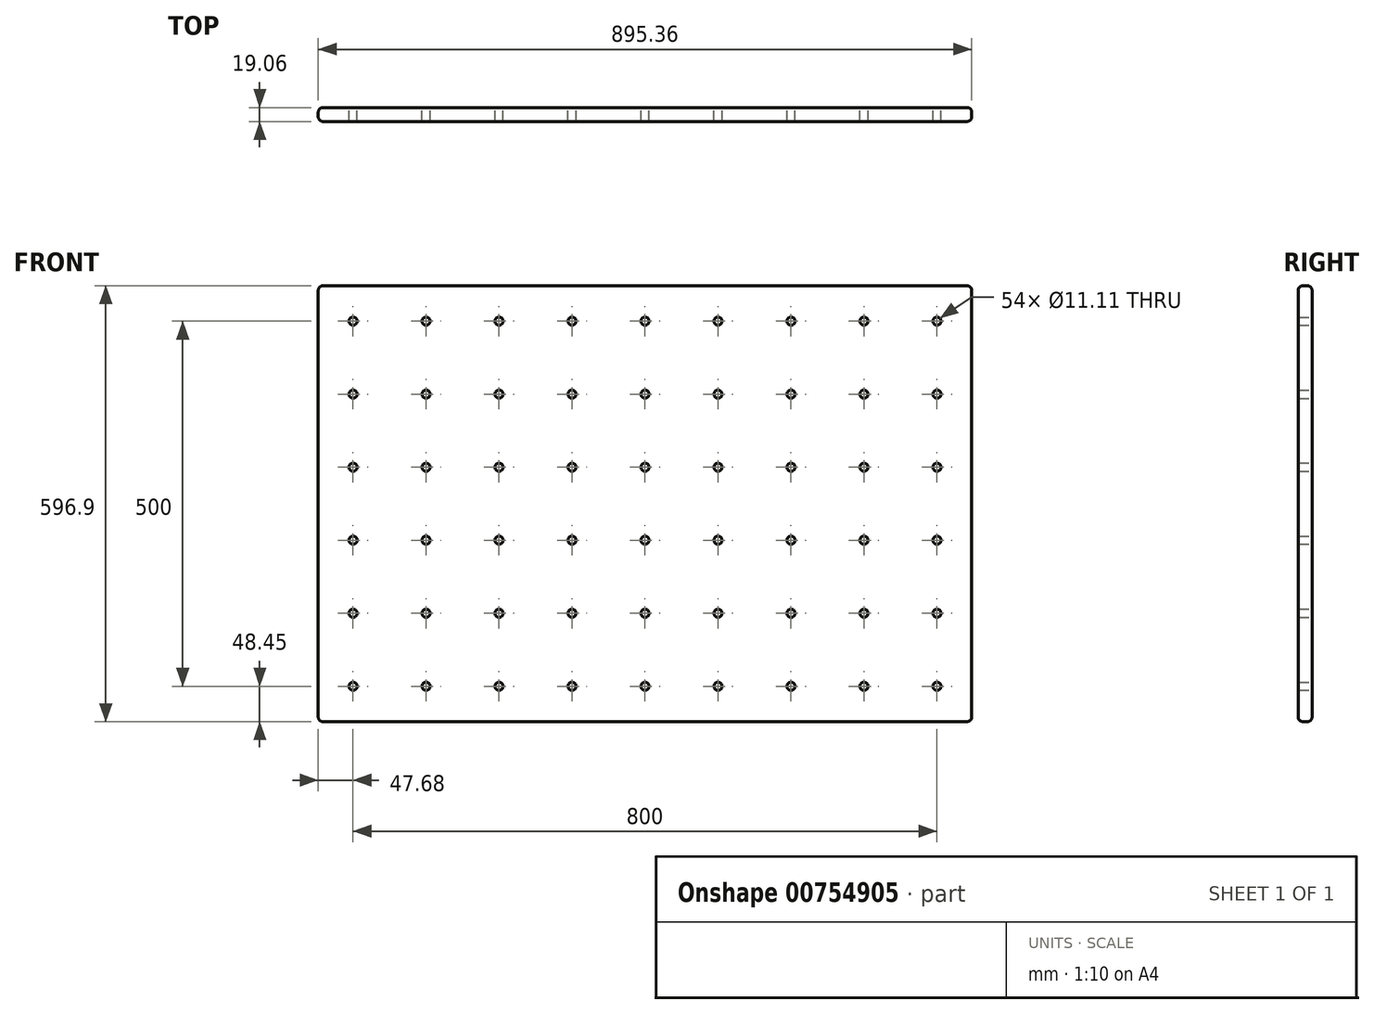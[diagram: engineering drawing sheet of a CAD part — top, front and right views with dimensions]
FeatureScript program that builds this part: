
annotation { "Feature Type Name" : "Feature", "Feature Type Description" : "" }
export const myFeature = defineFeature(function(context is Context, id is Id, definition is map)
    precondition{}
    {
        {
            var Q0;
            Q0=qCreatedBy(makeId("Front.planeOp"),FACE);
            var sketch = newSketch(context, id + "F0", { "sketchPlane" : qUnion([Q0])});
            skLineSegment(sketch, "E0.bottom", {"start": v(-447.68, 298.45) * mm, "end": v(447.68, 298.45) * mm});
            skLineSegment(sketch, "E0.top", {"start": v(-447.68, -298.45) * mm, "end": v(447.67, -298.45) * mm});
            skLineSegment(sketch, "E0.left", {"start": v(-447.68, 298.45) * mm, "end": v(-447.68, -298.45) * mm});
            skLineSegment(sketch, "E0.right", {"start": v(447.68, 298.45) * mm, "end": v(447.67, -298.45) * mm});
            skCircle(sketch, "E1", {"center": v(400, -250) * mm, "radius": 5.56 * mm});
            skCircle(sketch, "E2.0.1.0", {"center": v(400, -150) * mm, "radius": 5.56 * mm});
            skCircle(sketch, "E2.0.2.0", {"center": v(400, -50) * mm, "radius": 5.56 * mm});
            skCircle(sketch, "E2.0.3.0", {"center": v(400, 50) * mm, "radius": 5.56 * mm});
            skCircle(sketch, "E2.0.4.0", {"center": v(400, 150) * mm, "radius": 5.56 * mm});
            skCircle(sketch, "E2.0.5.0", {"center": v(400, 250) * mm, "radius": 5.56 * mm});
            skCircle(sketch, "E2.1.0.0", {"center": v(300, -250) * mm, "radius": 5.56 * mm});
            skCircle(sketch, "E2.1.1.0", {"center": v(300, -150) * mm, "radius": 5.56 * mm});
            skCircle(sketch, "E2.1.2.0", {"center": v(300, -50) * mm, "radius": 5.56 * mm});
            skCircle(sketch, "E2.1.3.0", {"center": v(300, 50) * mm, "radius": 5.56 * mm});
            skCircle(sketch, "E2.1.4.0", {"center": v(300, 150) * mm, "radius": 5.56 * mm});
            skCircle(sketch, "E2.1.5.0", {"center": v(300, 250) * mm, "radius": 5.56 * mm});
            skCircle(sketch, "E2.2.0.0", {"center": v(200, -250) * mm, "radius": 5.56 * mm});
            skCircle(sketch, "E2.2.1.0", {"center": v(200, -150) * mm, "radius": 5.56 * mm});
            skCircle(sketch, "E2.2.2.0", {"center": v(200, -50) * mm, "radius": 5.56 * mm});
            skCircle(sketch, "E2.2.3.0", {"center": v(200, 50) * mm, "radius": 5.56 * mm});
            skCircle(sketch, "E2.2.4.0", {"center": v(200, 150) * mm, "radius": 5.56 * mm});
            skCircle(sketch, "E2.2.5.0", {"center": v(200, 250) * mm, "radius": 5.56 * mm});
            skCircle(sketch, "E2.3.0.0", {"center": v(100, -250) * mm, "radius": 5.56 * mm});
            skCircle(sketch, "E2.3.1.0", {"center": v(100, -150) * mm, "radius": 5.56 * mm});
            skCircle(sketch, "E2.3.2.0", {"center": v(100, -50) * mm, "radius": 5.56 * mm});
            skCircle(sketch, "E2.3.3.0", {"center": v(100, 50) * mm, "radius": 5.56 * mm});
            skCircle(sketch, "E2.3.4.0", {"center": v(100, 150) * mm, "radius": 5.56 * mm});
            skCircle(sketch, "E2.3.5.0", {"center": v(100, 250) * mm, "radius": 5.56 * mm});
            skCircle(sketch, "E2.4.0.0", {"center": v(0, -250) * mm, "radius": 5.56 * mm});
            skCircle(sketch, "E2.4.1.0", {"center": v(0, -150) * mm, "radius": 5.56 * mm});
            skCircle(sketch, "E2.4.2.0", {"center": v(0, -50) * mm, "radius": 5.56 * mm});
            skCircle(sketch, "E2.4.3.0", {"center": v(0, 50) * mm, "radius": 5.56 * mm});
            skCircle(sketch, "E2.4.4.0", {"center": v(0, 150) * mm, "radius": 5.56 * mm});
            skCircle(sketch, "E2.4.5.0", {"center": v(0, 250) * mm, "radius": 5.56 * mm});
            skCircle(sketch, "E2.5.0.0", {"center": v(-100, -250) * mm, "radius": 5.56 * mm});
            skCircle(sketch, "E2.5.1.0", {"center": v(-100, -150) * mm, "radius": 5.56 * mm});
            skCircle(sketch, "E2.5.2.0", {"center": v(-100, -50) * mm, "radius": 5.56 * mm});
            skCircle(sketch, "E2.5.3.0", {"center": v(-100, 50) * mm, "radius": 5.56 * mm});
            skCircle(sketch, "E2.5.4.0", {"center": v(-100, 150) * mm, "radius": 5.56 * mm});
            skCircle(sketch, "E2.5.5.0", {"center": v(-100, 250) * mm, "radius": 5.56 * mm});
            skCircle(sketch, "E2.6.0.0", {"center": v(-200, -250) * mm, "radius": 5.56 * mm});
            skCircle(sketch, "E2.6.1.0", {"center": v(-200, -150) * mm, "radius": 5.56 * mm});
            skCircle(sketch, "E2.6.2.0", {"center": v(-200, -50) * mm, "radius": 5.56 * mm});
            skCircle(sketch, "E2.6.3.0", {"center": v(-200, 50) * mm, "radius": 5.56 * mm});
            skCircle(sketch, "E2.6.4.0", {"center": v(-200, 150) * mm, "radius": 5.56 * mm});
            skCircle(sketch, "E2.6.5.0", {"center": v(-200, 250) * mm, "radius": 5.56 * mm});
            skCircle(sketch, "E2.7.0.0", {"center": v(-300, -250) * mm, "radius": 5.56 * mm});
            skCircle(sketch, "E2.7.1.0", {"center": v(-300, -150) * mm, "radius": 5.56 * mm});
            skCircle(sketch, "E2.7.2.0", {"center": v(-300, -50) * mm, "radius": 5.56 * mm});
            skCircle(sketch, "E2.7.3.0", {"center": v(-300, 50) * mm, "radius": 5.56 * mm});
            skCircle(sketch, "E2.7.4.0", {"center": v(-300, 150) * mm, "radius": 5.56 * mm});
            skCircle(sketch, "E2.7.5.0", {"center": v(-300, 250) * mm, "radius": 5.56 * mm});
            skCircle(sketch, "E2.8.0.0", {"center": v(-400, -250) * mm, "radius": 5.56 * mm});
            skCircle(sketch, "E2.8.1.0", {"center": v(-400, -150) * mm, "radius": 5.56 * mm});
            skCircle(sketch, "E2.8.2.0", {"center": v(-400, -50) * mm, "radius": 5.56 * mm});
            skCircle(sketch, "E2.8.3.0", {"center": v(-400, 50) * mm, "radius": 5.56 * mm});
            skCircle(sketch, "E2.8.4.0", {"center": v(-400, 150) * mm, "radius": 5.56 * mm});
            skCircle(sketch, "E2.8.5.0", {"center": v(-400, 250) * mm, "radius": 5.56 * mm});
            skLineSegment(sketch, "E2.direction1", {"start": v(400, -250) * mm, "end": v(300, -250) * mm, "construction": true});
            skLineSegment(sketch, "E2.direction2", {"start": v(400, -250) * mm, "end": v(400, -150) * mm, "construction": true});
            skSolve(sketch);
        }
        {
            var Q0;
            Q0=makeQuery(id+"F0.imprint","IMPRINT",FACE,{"disambiguationData":[TD([[makeQuery(id+"F0.imprint","IMPRINT",EDGE,{"derivedFrom":sQuery(id+"F0.wireOp",EDGE,"E0.bottom")}),-1.0]])]});
            extrude(context, id + "F1", {"entities" : qUnion([Q0]), "endBound" : BoundingType.SYMMETRIC, "depth" : 19.05 * mm});
        }
        {
            var Q0;
            Q0=makeQuery(id+"F1.opExtrude","SWEPT_EDGE",EDGE,{"disambiguationData":[OSD([sQuery(id+"F0.wireOp",EDGE,"E0.bottom"),sQuery(id+"F0.wireOp",EDGE,"E0.left")])]});
            var Q1;
            Q1=makeQuery(id+"F1.opExtrude","CAP_EDGE",EDGE,{"disambiguationData":[OSD([sQuery(id+"F0.wireOp",EDGE,"E0.bottom")])],"isStart":true});
            var Q2;
            Q2=makeQuery(id+"F1.opExtrude","CAP_EDGE",EDGE,{"disambiguationData":[OSD([sQuery(id+"F0.wireOp",EDGE,"E0.left")])],"isStart":true});
            var Q3;
            Q3=makeQuery(id+"F1.opExtrude","CAP_EDGE",EDGE,{"disambiguationData":[OSD([sQuery(id+"F0.wireOp",EDGE,"E0.left")])],"isStart":false});
            var Q4;
            Q4=makeQuery(id+"F1.opExtrude","SWEPT_EDGE",EDGE,{"disambiguationData":[OSD([sQuery(id+"F0.wireOp",EDGE,"E0.bottom"),sQuery(id+"F0.wireOp",EDGE,"E0.right")])]});
            var Q5;
            Q5=makeQuery(id+"F1.opExtrude","CAP_EDGE",EDGE,{"disambiguationData":[OSD([sQuery(id+"F0.wireOp",EDGE,"E0.bottom")])],"isStart":false});
            var Q6;
            Q6=makeQuery(id+"F1.opExtrude","CAP_EDGE",EDGE,{"disambiguationData":[OSD([sQuery(id+"F0.wireOp",EDGE,"E0.right")])],"isStart":false});
            var Q7;
            Q7=makeQuery(id+"F1.opExtrude","CAP_EDGE",EDGE,{"disambiguationData":[OSD([sQuery(id+"F0.wireOp",EDGE,"E0.top")])],"isStart":false});
            var Q8;
            Q8=makeQuery(id+"F1.opExtrude","SWEPT_EDGE",EDGE,{"disambiguationData":[OSD([sQuery(id+"F0.wireOp",EDGE,"E0.top"),sQuery(id+"F0.wireOp",EDGE,"E0.left")])]});
            var Q9;
            Q9=makeQuery(id+"F1.opExtrude","CAP_EDGE",EDGE,{"disambiguationData":[OSD([sQuery(id+"F0.wireOp",EDGE,"E0.top")])],"isStart":true});
            var Q10;
            Q10=makeQuery(id+"F1.opExtrude","SWEPT_EDGE",EDGE,{"disambiguationData":[OSD([sQuery(id+"F0.wireOp",EDGE,"E0.top"),sQuery(id+"F0.wireOp",EDGE,"E0.right")])]});
            var Q11;
            Q11=makeQuery(id+"F1.opExtrude","CAP_EDGE",EDGE,{"disambiguationData":[OSD([sQuery(id+"F0.wireOp",EDGE,"E0.right")])],"isStart":true});
            fillet(context, id + "F2", {"entities" : qUnion([Q0, Q1, Q2, Q3, Q4, Q5, Q6, Q7, Q8, Q9, Q10, Q11]), "radius" : 6.35 * mm, "tangentPropagation" : true, "allowEdgeOverflow" : false});
        }
    });
